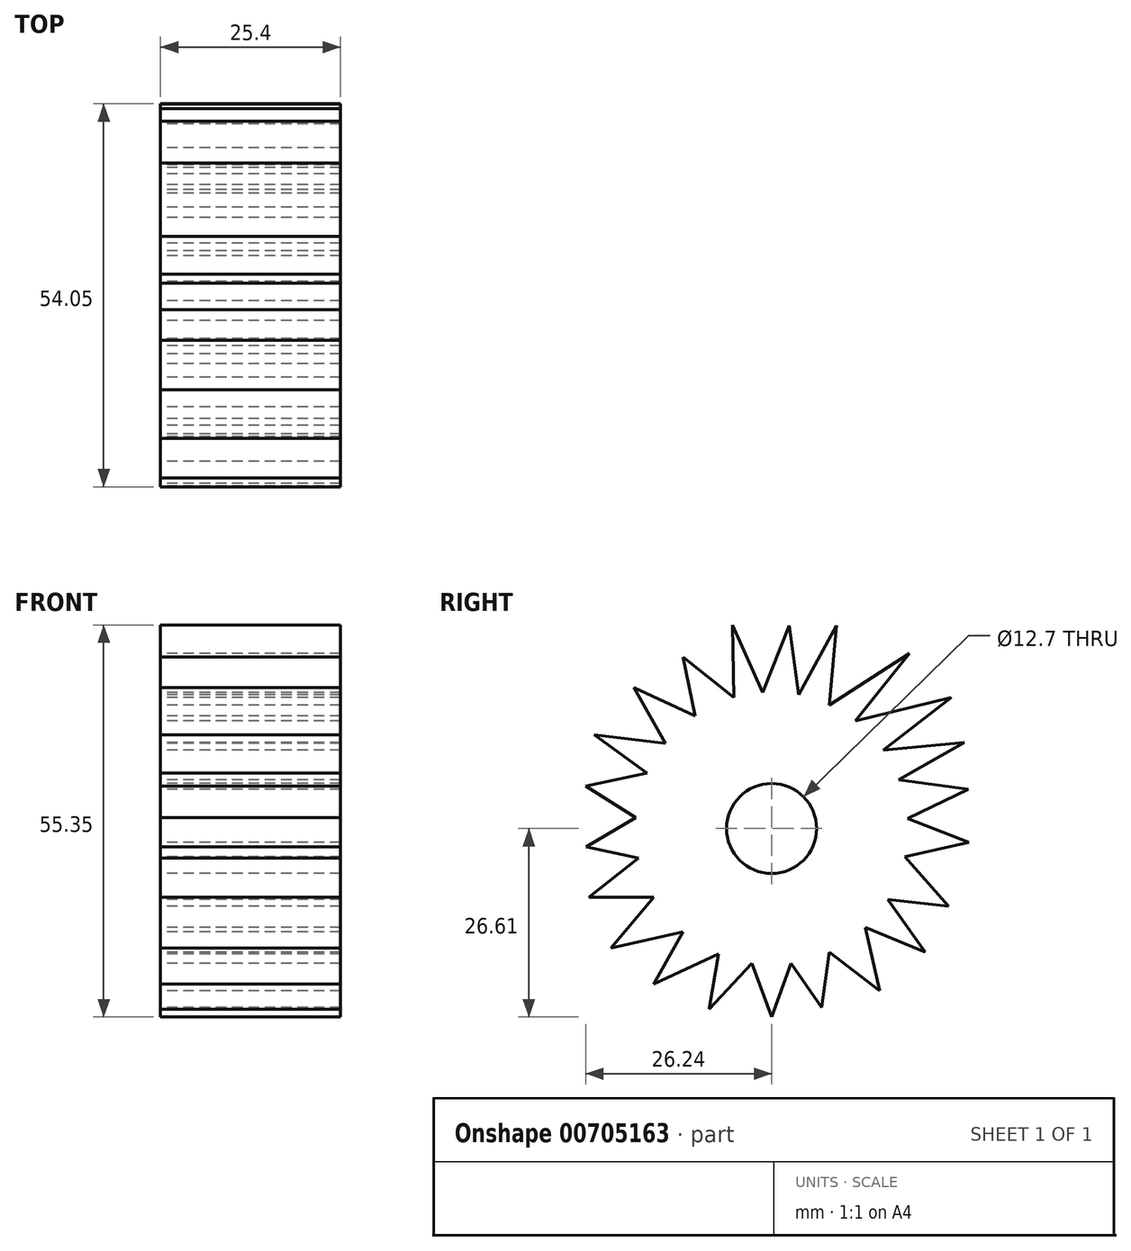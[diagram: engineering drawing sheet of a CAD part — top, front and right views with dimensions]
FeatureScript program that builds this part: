
annotation { "Feature Type Name" : "Feature", "Feature Type Description" : "" }
export const myFeature = defineFeature(function(context is Context, id is Id, definition is map)
    precondition{}
    {
        {
            var Q0;
            Q0=qCreatedBy(makeId("Right.planeOp"),FACE);
            var sketch = newSketch(context, id + "F0", { "sketchPlane" : qUnion([Q0])});
            skCircle(sketch, "E0", {"center": v(0, 0) * mm, "radius": 19.23 * mm});
            skCircle(sketch, "E1", {"center": v(0, 0) * mm, "radius": 6.35 * mm});
            skLineSegment(sketch, "E2", {"start": v(8.15, 17.42) * mm, "end": v(6.27, 18.18) * mm});
            skLineSegment(sketch, "E3", {"start": v(-5.34, 18.47) * mm, "end": v(-12.52, 24.24) * mm});
            skLineSegment(sketch, "E4", {"start": v(-12.52, 24.24) * mm, "end": v(-10.78, 15.92) * mm});
            skLineSegment(sketch, "E5", {"start": v(-10.78, 15.92) * mm, "end": v(-19.42, 19.9) * mm});
            skLineSegment(sketch, "E6", {"start": v(-19.42, 19.9) * mm, "end": v(-14.99, 12.05) * mm});
            skLineSegment(sketch, "E7", {"start": v(-14.99, 12.05) * mm, "end": v(-25, 13.24) * mm});
            skLineSegment(sketch, "E8", {"start": v(-25, 13.24) * mm, "end": v(-17.57, 7.8) * mm});
            skLineSegment(sketch, "E9", {"start": v(-17.57, 7.8) * mm, "end": v(-26.24, 6.01) * mm});
            skLineSegment(sketch, "E10", {"start": v(-26.24, 6.01) * mm, "end": v(-19.16, 1.58) * mm});
            skLineSegment(sketch, "E11", {"start": v(-19.16, 1.58) * mm, "end": v(-26.15, -2.6) * mm});
            skLineSegment(sketch, "E12", {"start": v(-26.15, -2.6) * mm, "end": v(-18.77, -4.17) * mm});
            skLineSegment(sketch, "E13", {"start": v(-18.77, -4.17) * mm, "end": v(-25.75, -9.7) * mm});
            skLineSegment(sketch, "E14", {"start": v(-25.75, -9.7) * mm, "end": v(-16.6, -9.7) * mm});
            skLineSegment(sketch, "E15", {"start": v(-16.6, -9.7) * mm, "end": v(-22.66, -16.86) * mm});
            skLineSegment(sketch, "E16", {"start": v(-22.66, -16.86) * mm, "end": v(-12.52, -14.6) * mm});
            skLineSegment(sketch, "E17", {"start": v(-12.52, -14.6) * mm, "end": v(-16.6, -21.92) * mm});
            skLineSegment(sketch, "E18", {"start": v(-16.6, -21.92) * mm, "end": v(-7.45, -17.73) * mm});
            skLineSegment(sketch, "E19", {"start": v(-7.45, -17.73) * mm, "end": v(-8.84, -25.5) * mm});
            skLineSegment(sketch, "E20", {"start": v(-8.84, -25.5) * mm, "end": v(-2.76, -19.03) * mm});
            skLineSegment(sketch, "E21", {"start": v(-2.76, -19.03) * mm, "end": v(0, -26.61) * mm});
            skLineSegment(sketch, "E22", {"start": v(0, -26.61) * mm, "end": v(2.77, -19.03) * mm});
            skLineSegment(sketch, "E23", {"start": v(2.77, -19.03) * mm, "end": v(7.08, -25.25) * mm});
            skLineSegment(sketch, "E24", {"start": v(7.08, -25.25) * mm, "end": v(8.16, -17.41) * mm});
            skLineSegment(sketch, "E25", {"start": v(8.16, -17.41) * mm, "end": v(15.22, -22.9) * mm});
            skLineSegment(sketch, "E26", {"start": v(15.22, -22.9) * mm, "end": v(13.21, -13.97) * mm});
            skLineSegment(sketch, "E27", {"start": v(13.21, -13.97) * mm, "end": v(21.64, -17.41) * mm});
            skLineSegment(sketch, "E28", {"start": v(21.64, -17.41) * mm, "end": v(16.4, -10.04) * mm});
            skLineSegment(sketch, "E29", {"start": v(16.4, -10.04) * mm, "end": v(24.97, -10.94) * mm});
            skLineSegment(sketch, "E30", {"start": v(24.97, -10.94) * mm, "end": v(18.8, -4) * mm});
            skLineSegment(sketch, "E31", {"start": v(18.8, -4) * mm, "end": v(27.8, -1.93) * mm});
            skLineSegment(sketch, "E32", {"start": v(27.8, -1.93) * mm, "end": v(19.17, 1.4) * mm});
            skLineSegment(sketch, "E33", {"start": v(19.17, 1.4) * mm, "end": v(27.77, 5.54) * mm});
            skLineSegment(sketch, "E34", {"start": v(27.77, 5.54) * mm, "end": v(17.95, 6.9) * mm});
            skLineSegment(sketch, "E35", {"start": v(17.95, 6.9) * mm, "end": v(27.16, 12.15) * mm});
            skLineSegment(sketch, "E36", {"start": v(27.16, 12.15) * mm, "end": v(15.74, 11.05) * mm});
            skLineSegment(sketch, "E37", {"start": v(15.74, 11.05) * mm, "end": v(25.34, 18.47) * mm});
            skLineSegment(sketch, "E38", {"start": v(25.34, 18.47) * mm, "end": v(11.8, 15.2) * mm});
            skLineSegment(sketch, "E39", {"start": v(11.8, 15.2) * mm, "end": v(19.44, 24.72) * mm});
            skLineSegment(sketch, "E40", {"start": v(-1.26, 19.19) * mm, "end": v(2.5, 28.66) * mm});
            skLineSegment(sketch, "E41", {"start": v(2.5, 28.66) * mm, "end": v(3.8, 18.85) * mm});
            skLineSegment(sketch, "E42", {"start": v(3.8, 18.85) * mm, "end": v(9.13, 28.66) * mm});
            skLineSegment(sketch, "E43", {"start": v(9.13, 28.66) * mm, "end": v(8.15, 17.42) * mm});
            skLineSegment(sketch, "E44", {"start": v(-1.26, 19.19) * mm, "end": v(-5.54, 28.74) * mm});
            skLineSegment(sketch, "E45", {"start": v(-5.54, 28.74) * mm, "end": v(-5.34, 18.47) * mm});
            skLineSegment(sketch, "E46", {"start": v(8.15, 17.42) * mm, "end": v(19.44, 24.72) * mm});
            skSolve(sketch);
        }
        {
            var Q0;
            Q0 = qSketchRegion(id + "F0", true);
            extrude(context, id + "F1", {"entities" : qUnion([Q0]), "depth" : 12.7 * mm, "offsetDistance" : 25.4 * mm});
        }
        {
            var Q0;
            Q0 = qSketchRegion(id + "F0", true);
            extrude(context, id + "F2", {"entities" : qUnion([Q0]), "operationType" : NewBodyOperationType.ADD, "depth" : 25.4 * mm, "offsetDistance" : 25.4 * mm});
        }
    });
